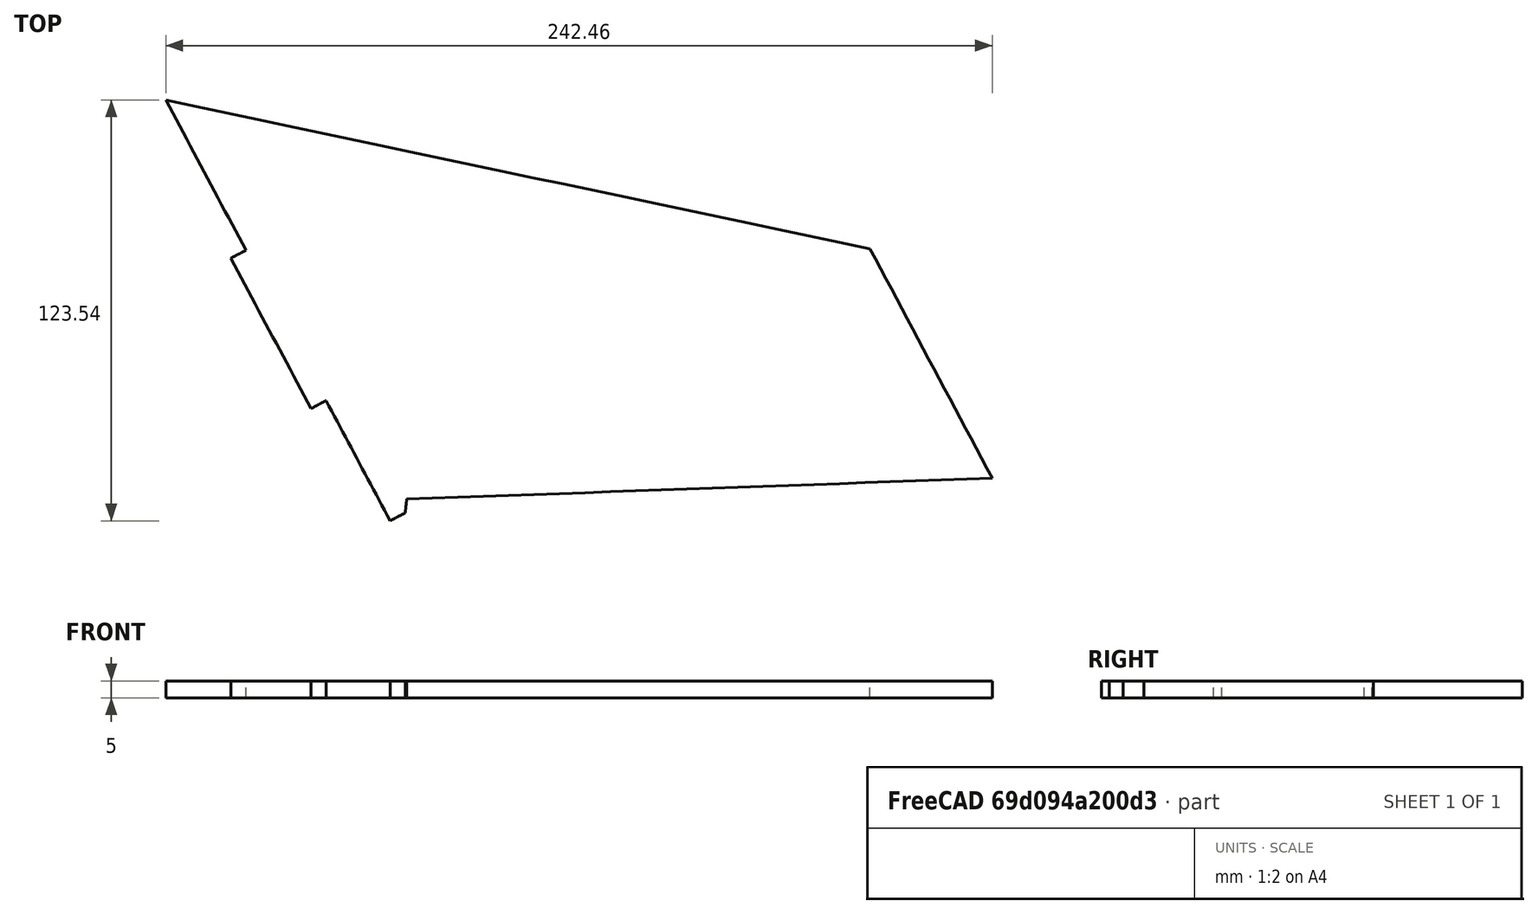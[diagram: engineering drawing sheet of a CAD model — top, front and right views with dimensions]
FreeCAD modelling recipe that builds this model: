
FCSTD DOCUMENT  (FreeCAD 0.19R)
Label: F-35_v2_parts_8
License: All rights reserved
LicenseURL: http://en.wikipedia.org/wiki/All_rights_reserved
objects: App::DocumentObjectGroup×2, PartDesign::CoordinateSystem×2, App::FeaturePython×1, Sketcher::SketchObject×1, PartDesign::Pad×1, PartDesign::Body×1, App::Part×1
note: 6 computed .brp shape members not serialized (recipe doc carries the construction recipe); baked Part::Feature solids carry a one-line shape summary decoded from their .brp

FEATURE [App::DocumentObjectGroup] Parts
FEATURE [PartDesign::CoordinateSystem] LCS_Origin
  AttacherType = Attacher::AttachEngine3D
  MapMode = 2
  Support = -> [X_Axis]
FEATURE [App::DocumentObjectGroup] Constraints
FEATURE [App::FeaturePython] Variables  # WARN: FeaturePython — macro-defined, semantics opaque (R4)
FEATURE [Sketcher::SketchObject] Sketch007
  FullyConstrained = false
  sketch-geometry (10):
    g0: BSplineCurve PolesCount=2 KnotsCount=2 Degree=1 IsPeriodic=0
    g1: BSplineCurve PolesCount=2 KnotsCount=2 Degree=1 IsPeriodic=0
    g2: BSplineCurve PolesCount=2 KnotsCount=2 Degree=1 IsPeriodic=0
    g3: BSplineCurve PolesCount=2 KnotsCount=2 Degree=1 IsPeriodic=0
    g4: BSplineCurve PolesCount=2 KnotsCount=2 Degree=1 IsPeriodic=0
    g5: BSplineCurve PolesCount=2 KnotsCount=2 Degree=1 IsPeriodic=0
    g6: BSplineCurve PolesCount=2 KnotsCount=2 Degree=1 IsPeriodic=0
    g7: BSplineCurve PolesCount=2 KnotsCount=2 Degree=1 IsPeriodic=0
    g8: BSplineCurve PolesCount=2 KnotsCount=2 Degree=1 IsPeriodic=0
    g9: BSplineCurve PolesCount=2 KnotsCount=2 Degree=1 IsPeriodic=0
FEATURE [PartDesign::Pad] Pad006
  Direction = (1,1,1)
  Length = 5
  Length2 = 100
  Profile = -> Sketch007
  Type = 0
FEATURE [PartDesign::Body] Body007  label="Part8"
  Group = -> [Sketch007,Pad006]
  Origin = -> Origin008
  Tip = -> Pad006
FEATURE [PartDesign::CoordinateSystem] LCS_1
  AttacherType = Attacher::AttachEngine3D
  AttachmentOffset = pos=(0,0,0) rot=(0,0.020107,-0.999798;-0.331613rad)
  MapMode = 45
  Placement = pos=(421.988,-579.401,2.5) rot=(0.609041,0.71635,0.340457;4.57343rad)
  Support = -> [Pad006]
FEATURE [App::Part] Model
  Configuration = 0
  Group = -> [LCS_Origin,Constraints,Variables,Body007,LCS_1]
  Origin = -> Origin
  Type = Assembly4 Model
